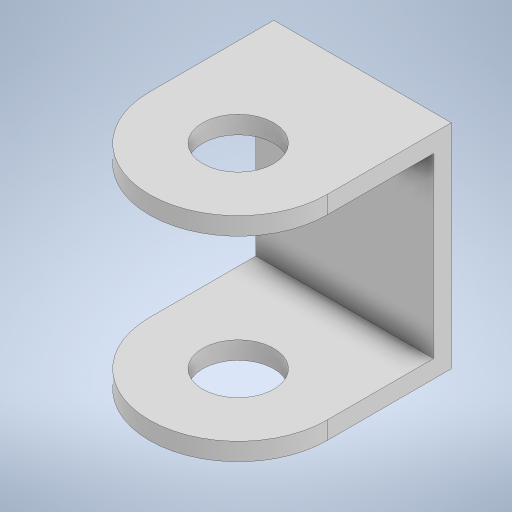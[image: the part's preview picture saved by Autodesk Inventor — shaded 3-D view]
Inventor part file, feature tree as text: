
AUTODESK INVENTOR PART (.ipt)
format: ipt  version: 2023.2 (Build 272271000, 271)  size: 307,712 bytes
history: native  units: mm
features: sketch x2, extrude x1
ambient origin geometry x8: Origin, YZ Plane, XZ Plane, XY Plane, X Axis, Y Axis, Z Axis, Center Point
bodies: Body1 (feature_tree)
feature tree (3):
  extrude  "Extrusion18"  Depth=10.0mm
  sketch  "Sketch2"  dims[d230=10.0mm d231=7.0mm]
  sketch  "Sketch16"  dims[d232=5.0mm d234=4.0mm d235=1.0mm d236=0.0mm d237=1.0mm d238=10.0mm d239=0.0mm d244=4.0mm d245=1.0mm d246=0.0mm d9=0.5mm d10=0.872665mm d11=0.5mm d12=0.872665mm d13=0.5mm d14=0.872665mm d27=0.5mm d28=0.872665mm d29=0.5mm d30=0.872665mm d88=0.5mm d89=0.872665mm d90=0.5mm d91=0.872665mm d116=0.5mm d117=0.872665mm d118=0.5mm d119=0.872665mm d154=0.5mm d155=0.872665mm d156=0.5mm d157=0.872665mm d181=0.5mm d182=0.872665mm d183=0.5mm d184=0.872665mm d221=0.5mm d222=0.872665mm d223=0.5mm d224=0.872665mm]
